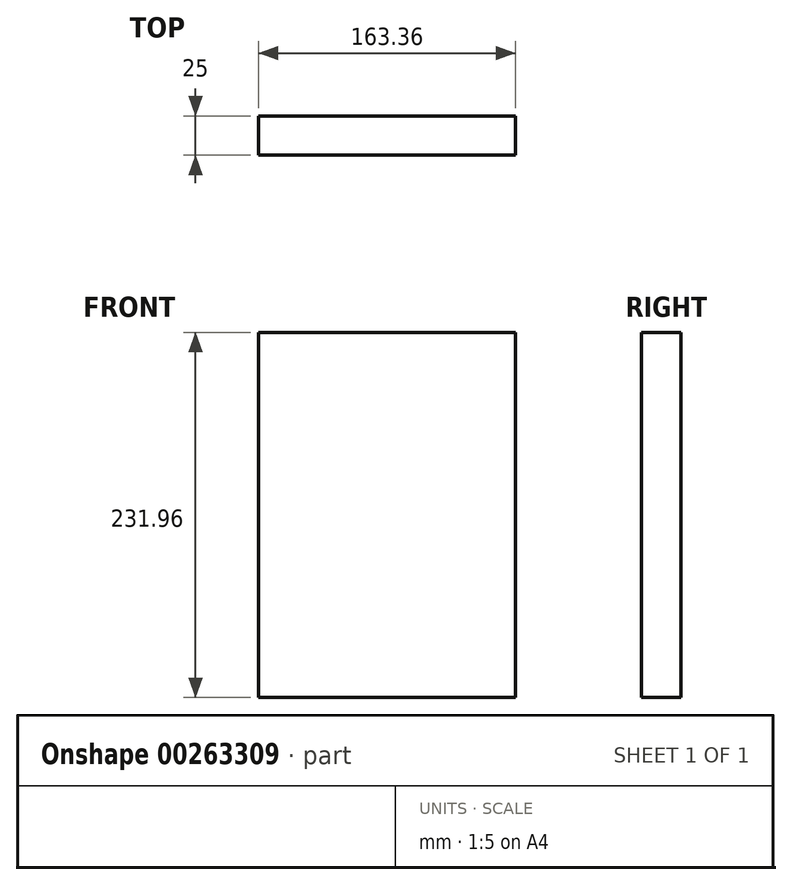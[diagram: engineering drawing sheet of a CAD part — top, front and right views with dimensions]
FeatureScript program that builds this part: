
annotation { "Feature Type Name" : "Feature", "Feature Type Description" : "" }
export const myFeature = defineFeature(function(context is Context, id is Id, definition is map)
    precondition{}
    {
        {
            var Q0;
            Q0=qCreatedBy(makeId("Front.planeOp"),FACE);
            var sketch = newSketch(context, id + "F0", { "sketchPlane" : qUnion([Q0])});
            skLineSegment(sketch, "E0.bottom", {"start": v(81.68, 115.98) * mm, "end": v(-81.68, 115.98) * mm});
            skLineSegment(sketch, "E0.top", {"start": v(81.68, -115.98) * mm, "end": v(-81.68, -115.98) * mm});
            skLineSegment(sketch, "E0.left", {"start": v(81.68, 115.98) * mm, "end": v(81.68, -115.98) * mm});
            skLineSegment(sketch, "E0.right", {"start": v(-81.68, 115.98) * mm, "end": v(-81.68, -115.98) * mm});
            skPoint(sketch, "E0.middle", {"position": v(0, 0) * mm});
            skSolve(sketch);
        }
        {
            var Q0;
            Q0=makeQuery(id+"F0.imprint","IMPRINT",FACE,{"disambiguationData":[TD([[makeQuery(id+"F0.imprint","IMPRINT",EDGE,{"derivedFrom":sQuery(id+"F0.wireOp",EDGE,"E0.bottom")}),1.0]])]});
            extrude(context, id + "F1", {"entities" : qUnion([Q0]), "depth" : 25 * mm});
        }
    });
